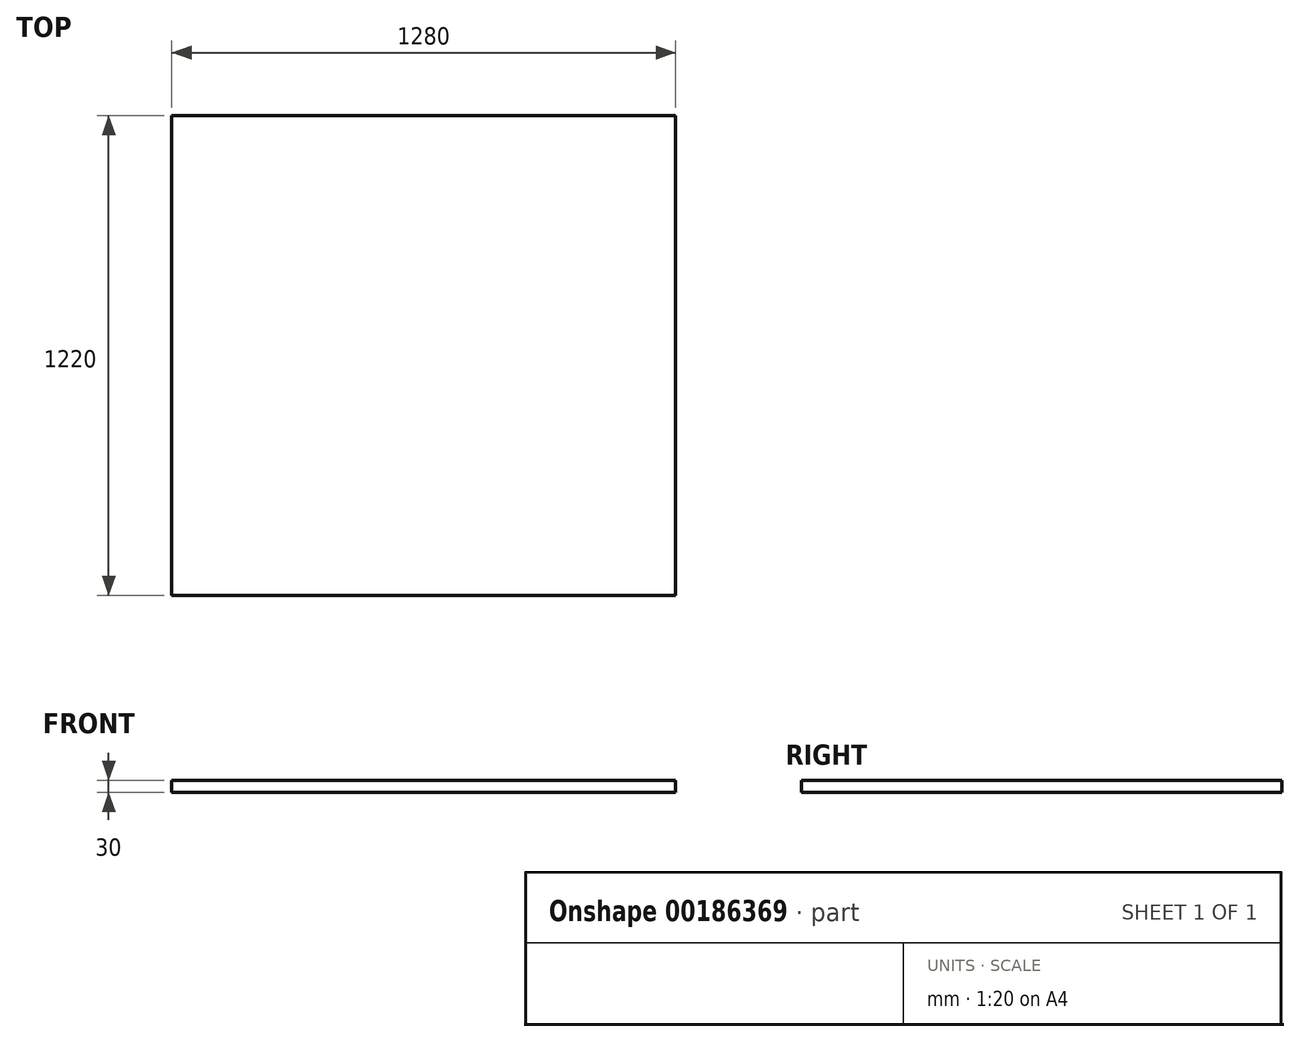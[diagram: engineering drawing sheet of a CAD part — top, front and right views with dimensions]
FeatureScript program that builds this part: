
annotation { "Feature Type Name" : "Feature", "Feature Type Description" : "" }
export const myFeature = defineFeature(function(context is Context, id is Id, definition is map)
    precondition{}
    {
        {
            var Q0;
            Q0=qCreatedBy(makeId("Top.planeOp"),FACE);
            var sketch = newSketch(context, id + "F0", { "sketchPlane" : qUnion([Q0])});
            skLineSegment(sketch, "E0.bottom", {"start": v(-1280, 1220) * mm, "end": v(0, 1220) * mm});
            skLineSegment(sketch, "E0.top", {"start": v(-1280, 0) * mm, "end": v(0, 0) * mm});
            skLineSegment(sketch, "E0.left", {"start": v(-1280, 1220) * mm, "end": v(-1280, 0) * mm});
            skLineSegment(sketch, "E0.right", {"start": v(0, 1220) * mm, "end": v(0, 0) * mm});
            skSolve(sketch);
        }
        {
            var Q0;
            Q0 = qSketchRegion(id + "F0", true);
            extrude(context, id + "F1", {"entities" : qUnion([Q0]), "depth" : 30 * mm});
        }
    });
